# Revit family: Контроллер биометрический PERCo_CL15
name_source: partatom
category: Охранная сигнализация
units: mm (PartAtom-declared; Revit-internal decimal feet)

## family parameters
Общий = Нет
Основа = Грань
При загрузке вырезать с полостями = Нет
Размер круглого соединителя = Использовать диаметр
Сохранять ориентацию аннотаций = Да
Тип детали = Нормальный
Точка расчета площади = Нет

## types (1)
- CL15
    ADSK_URL страницы изделия = https://www.perco.ru
    ADSK_Единица измерения = шт.
    ADSK_Завод-изготовитель = PERCo
    ADSK_Количество = 1
    ADSK_Масса_Текст = не более 0,3 кг
    ADSK_Материал наименование = Корпус выполнен из ударопрочного АБС-пластика
    ADSK_Наименование = Биометрический контроллер PERCo-CL15 со встроенным сканером отпечатков пальцев и RFID-считывателем карт доступа
    ADSK_Наименование краткое = Биометрический контроллер CL15
    ADSK_Напряжение = 12 В
    ADSK_Номинальная мощность = 5 В·А
    ADSK_Ток = 0 А
    Габаритные размеры = 170×70×51 мм
    Кол-во выносных считывателей = Не предусмотрено
    Кол-во контроллеров 2-го уровня = Не предусмотрено
    Кол-во подключаемых замков = 1
    Кол-во подключаемых турникетов = 1 (одно направление)
    Кол-во пользователей = до 50 000
    Кол-во событий = до 150 000
    Наличие встроенного считывателя = Да
    Наличие сканера отпечатка пальцев = Да
    Отметка по умолчанию = 1500 мм
    Подключение к электросети = 220В
    Степень защиты оболочки = IP50
    Температура использования = от -10°С до +40°С
    Тип интерфейса = Ethernet
    Формат читаемых карт = Mifare, EMM, HID Prox
